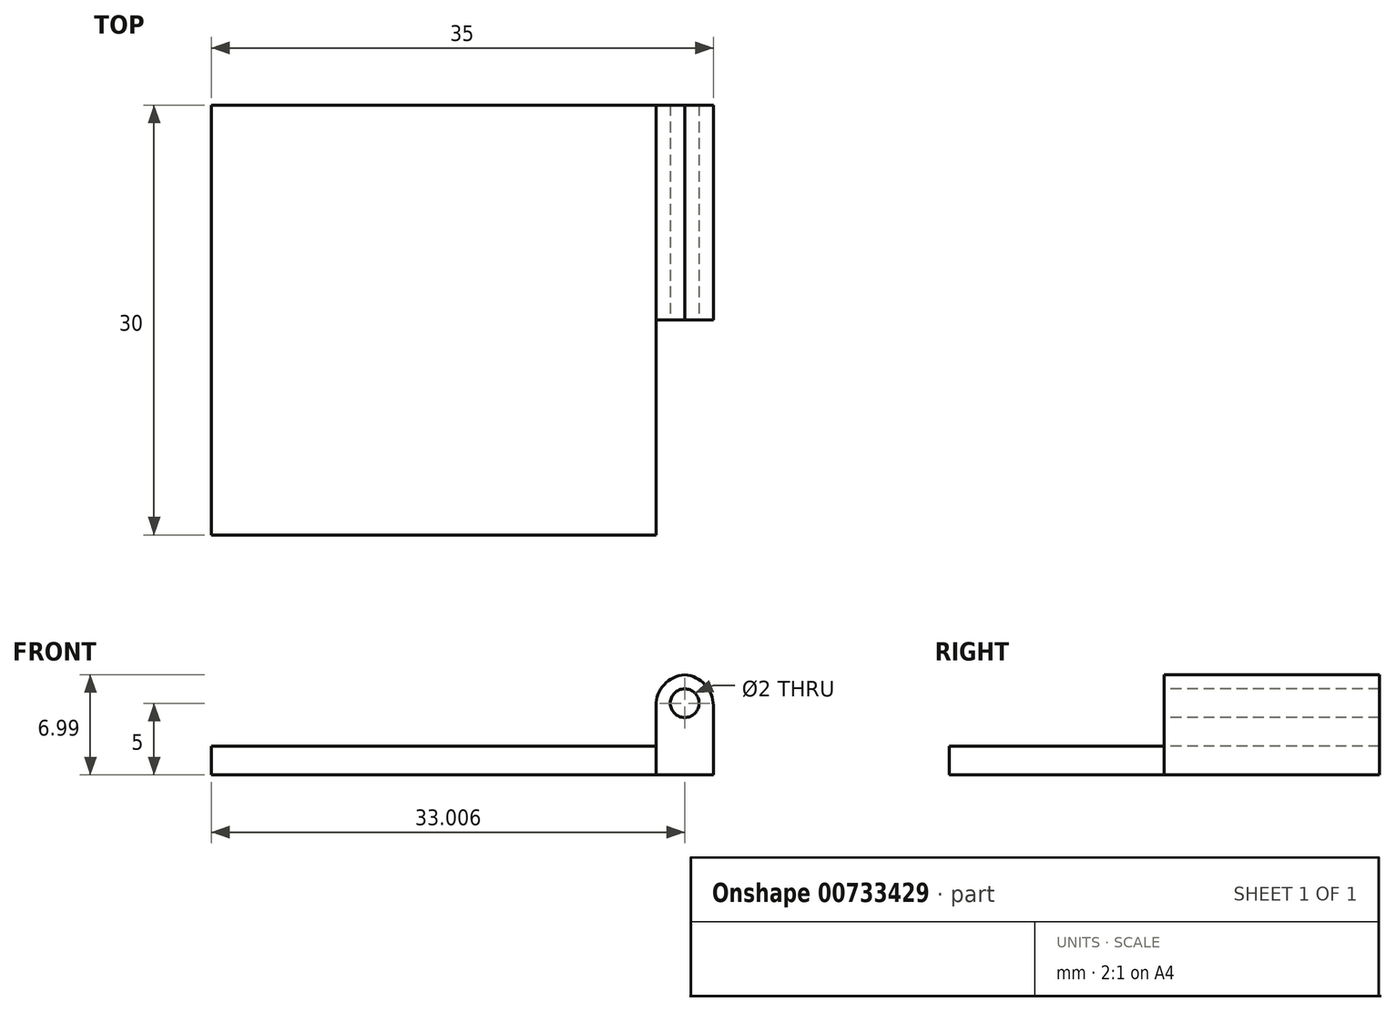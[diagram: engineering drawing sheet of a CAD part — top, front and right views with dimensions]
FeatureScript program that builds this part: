
annotation { "Feature Type Name" : "Feature", "Feature Type Description" : "" }
export const myFeature = defineFeature(function(context is Context, id is Id, definition is map)
    precondition{}
    {
        {
            var Q0;
            Q0=qCreatedBy(makeId("Top.planeOp"),FACE);
            var sketch = newSketch(context, id + "F0", { "sketchPlane" : qUnion([Q0])});
            skLineSegment(sketch, "E0.bottom", {"start": v(0, -15) * mm, "end": v(-35, -15) * mm});
            skLineSegment(sketch, "E0.top", {"start": v(0, 15) * mm, "end": v(-35, 15) * mm});
            skLineSegment(sketch, "E0.left", {"start": v(0, -15) * mm, "end": v(0, 15) * mm});
            skLineSegment(sketch, "E0.right", {"start": v(-35, -15) * mm, "end": v(-35, 15) * mm});
            skSolve(sketch);
        }
        {
            var Q0;
            Q0=qSketchRegion(id+"F0",true);
            extrude(context, id + "F1", {"entities" : qUnion([Q0]), "depth" : 2 * mm, "offsetDistance" : 25 * mm});
        }
        {
            var Q0;
            Q0=makeQuery(id+"F1.opExtrude","CAP_FACE",FACE,{"disambiguationData":[OSD([sQuery(id+"F0.wireOp",EDGE,"E0.bottom"),sQuery(id+"F0.wireOp",EDGE,"E0.top"),sQuery(id+"F0.wireOp",EDGE,"E0.left"),sQuery(id+"F0.wireOp",EDGE,"E0.right")])],"isStart":false});
            var sketch = newSketch(context, id + "F2", { "sketchPlane" : qUnion([Q0])});
            skLineSegment(sketch, "E1.bottom", {"start": v(0, 15) * mm, "end": v(0, 15) * mm});
            skLineSegment(sketch, "E1.top", {"start": v(0, 0) * mm, "end": v(0, 0) * mm});
            skLineSegment(sketch, "E1.left", {"start": v(0, 15) * mm, "end": v(0, 0) * mm});
            skLineSegment(sketch, "E1.right", {"start": v(0, 15) * mm, "end": v(0, 0) * mm});
            skLineSegment(sketch, "E2.bottom", {"start": v(0, 15) * mm, "end": v(-4, 15) * mm});
            skLineSegment(sketch, "E2.top", {"start": v(0, 0) * mm, "end": v(-4, 0) * mm});
            skLineSegment(sketch, "E2.right", {"start": v(-4, 15) * mm, "end": v(-4, 0) * mm});
            skSolve(sketch);
        }
        {
            var Q0;
            Q0=makeQuery(id+"F2.imprint","IMPRINT",FACE,{"disambiguationData":[TD([[makeQuery(id+"F2.imprint","IMPRINT",EDGE,{"derivedFrom":sQuery(id+"F2.wireOp",EDGE,"E2.bottom")}),1.0]])]});
            extrude(context, id + "F3", {"entities" : qUnion([Q0]), "operationType" : NewBodyOperationType.ADD, "depth" : 5 * mm, "offsetDistance" : 25 * mm});
        }
        {
            var Q0;
            Q0=makeQuery(id+"F3.opExtrude","SWEPT_FACE",FACE,{"disambiguationData":[OSD([sQuery(id+"F2.wireOp",EDGE,"E2.top")])]});
            var sketch = newSketch(context, id + "F4", { "sketchPlane" : qUnion([Q0])});
            skCircle(sketch, "E3", {"center": v(-2, 5) * mm, "radius": 1 * mm});
            skSolve(sketch);
        }
        {
            var Q0;
            Q0=qSketchRegion(id+"F4",true);
            extrude(context, id + "F5", {"entities" : qUnion([Q0]), "operationType" : NewBodyOperationType.REMOVE, "oppositeDirection" : true, "depth" : 25 * mm, "offsetDistance" : 25 * mm});
        }
        {
            var Q0;
            Q0=makeQuery(id+"F3.opExtrude","CAP_EDGE",EDGE,{"disambiguationData":[OSD([sQuery(id+"F2.wireOp",EDGE,"E2.right")])],"isStart":false});
            var Q1;
            Q1=makeQuery(id+"F3.opExtrude","CAP_EDGE",EDGE,{"disambiguationData":[OSD([sQuery(id+"F2.wireOp",EDGE,"E1.left")])],"isStart":false});
            fillet(context, id + "F6", {"entities" : qUnion([Q0, Q1]), "radius" : 2.17 * mm, "tangentPropagation" : true, "allowEdgeOverflow" : false});
        }
        {
            var Q0;
            Q0=makeQuery(id+"F1.opExtrude","CAP_FACE",FACE,{"disambiguationData":[OSD([sQuery(id+"F0.wireOp",EDGE,"E0.bottom"),sQuery(id+"F0.wireOp",EDGE,"E0.top"),sQuery(id+"F0.wireOp",EDGE,"E0.left"),sQuery(id+"F0.wireOp",EDGE,"E0.right")])],"isStart":false});
            var sketch = newSketch(context, id + "F7", { "sketchPlane" : qUnion([Q0])});
            skLineSegment(sketch, "E4.bottom", {"start": v(0, 0) * mm, "end": v(-4, 0) * mm});
            skLineSegment(sketch, "E4.top", {"start": v(0, -15) * mm, "end": v(-4, -15) * mm});
            skLineSegment(sketch, "E4.left", {"start": v(0, 0) * mm, "end": v(0, -15) * mm});
            skLineSegment(sketch, "E4.right", {"start": v(-4, 0) * mm, "end": v(-4, -15) * mm});
            skSolve(sketch);
        }
        {
            var Q0;
            Q0 = qSketchRegion(id + "F7", true);
            extrude(context, id + "F8", {"entities" : qUnion([Q0]), "operationType" : NewBodyOperationType.REMOVE, "oppositeDirection" : true, "depth" : 25 * mm, "offsetDistance" : 25 * mm});
        }
    });
